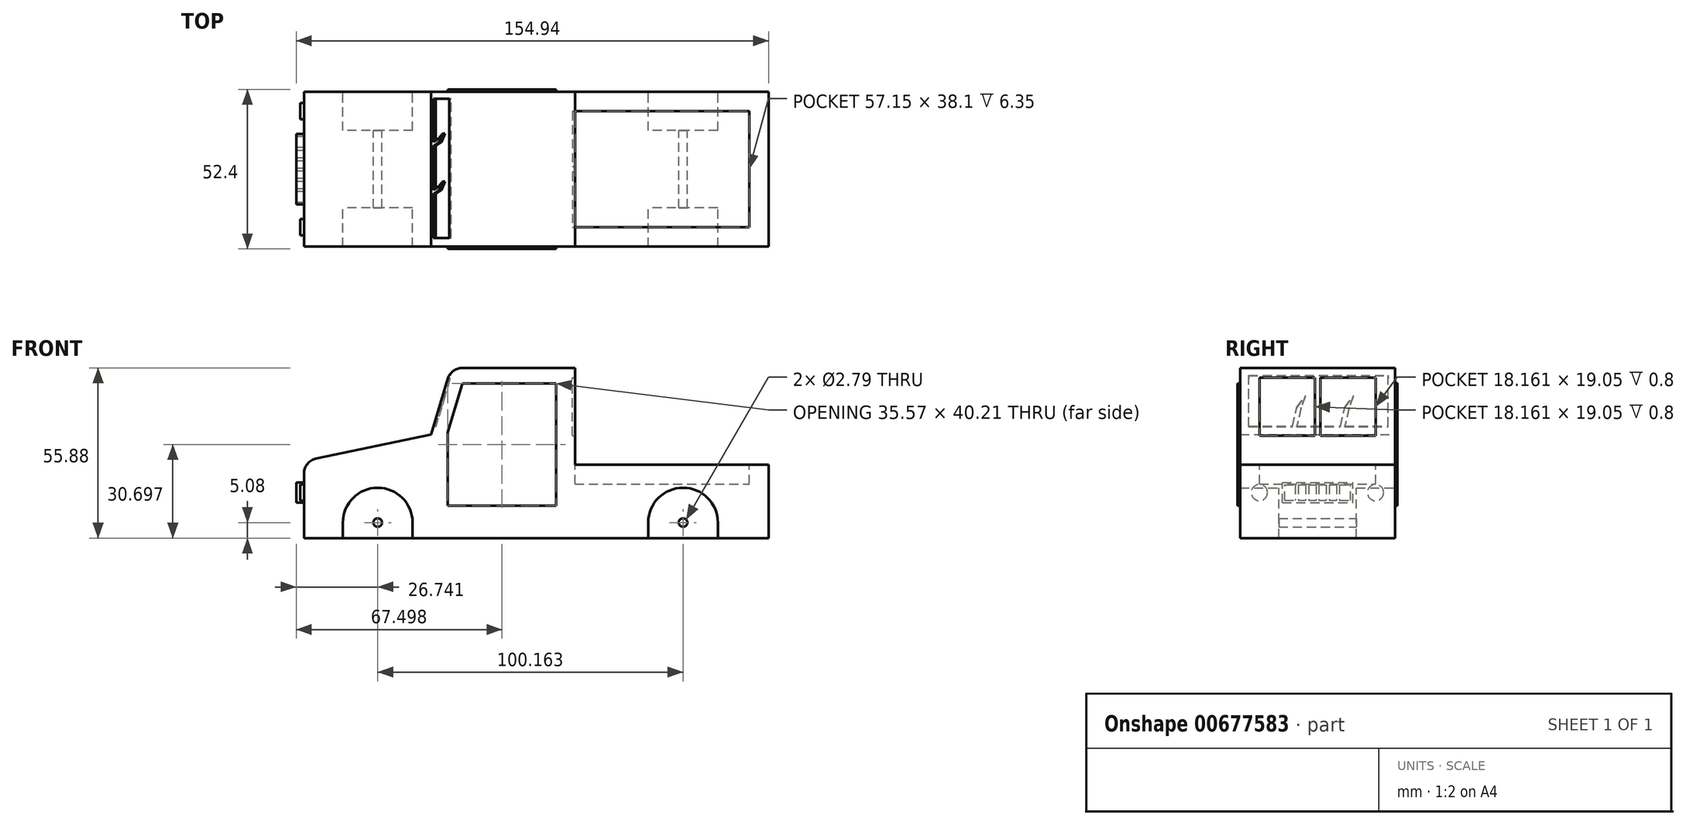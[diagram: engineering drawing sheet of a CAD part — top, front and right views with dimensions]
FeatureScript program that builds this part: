
annotation { "Feature Type Name" : "Feature", "Feature Type Description" : "" }
export const myFeature = defineFeature(function(context is Context, id is Id, definition is map)
    precondition{}
    {
        {
            var Q0;
            Q0=qCreatedBy(makeId("Front.planeOp"),FACE);
            var sketch = newSketch(context, id + "F0", { "sketchPlane" : qUnion([Q0])});
            skLineSegment(sketch, "E0", {"start": v(-68.75, 0) * mm, "end": v(83.65, 0) * mm});
            skLineSegment(sketch, "E1", {"start": v(83.65, 0) * mm, "end": v(83.65, 19.05) * mm});
            skLineSegment(sketch, "E2", {"start": v(83.65, 19.05) * mm, "end": v(20.15, 19.05) * mm});
            skLineSegment(sketch, "E3", {"start": v(20.15, 19.05) * mm, "end": v(20.15, 50.8) * mm});
            skLineSegment(sketch, "E4", {"start": v(20.15, 50.8) * mm, "end": v(-20.49, 50.8) * mm});
            skLineSegment(sketch, "E5", {"start": v(-20.49, 50.8) * mm, "end": v(-27.1, 28.92) * mm});
            skLineSegment(sketch, "E6", {"start": v(-68.75, 0) * mm, "end": v(-68.75, 20.2) * mm});
            skLineSegment(sketch, "E7", {"start": v(-68.75, 20.2) * mm, "end": v(-27.1, 28.92) * mm});
            skArc(sketch, "E8", {"start": v(-33.12, 0) * mm, "mid": v(-44.55, 11.43) * mm, "end": v(-55.98, 0) * mm});
            skArc(sketch, "E9", {"start": v(67.04, 0) * mm, "mid": v(55.61, 11.43) * mm, "end": v(44.18, 0) * mm});
            skSolve(sketch);
        }
        {
            var Q0;
            Q0 = qSketchRegion(id + "F0", true);
            extrude(context, id + "F1", {"entities" : qUnion([Q0]), "depth" : 50.8 * mm, "offsetDistance" : 25.4 * mm});
        }
        {
            var Q0;
            Q0=makeQuery(id+"F1.opExtrude","SWEPT_FACE",FACE,{"disambiguationData":[OSD([sQuery(id+"F0.wireOp",EDGE,"E2")])]});
            var sketch = newSketch(context, id + "F2", { "sketchPlane" : qUnion([Q0])});
            skLineSegment(sketch, "E10", {"start": v(20.15, -6.35) * mm, "end": v(77.3, -6.35) * mm});
            skLineSegment(sketch, "E11", {"start": v(77.3, -6.35) * mm, "end": v(77.3, -44.45) * mm});
            skLineSegment(sketch, "E12", {"start": v(77.3, -44.45) * mm, "end": v(20.15, -44.45) * mm});
            skLineSegment(sketch, "E13", {"start": v(20.15, -44.45) * mm, "end": v(20.15, -6.35) * mm});
            skSolve(sketch);
        }
        {
            var Q0;
            Q0=makeQuery(id+"F2.imprint","IMPRINT",FACE,{"disambiguationData":[TD([[makeQuery(id+"F2.imprint","IMPRINT",EDGE,{"derivedFrom":sQuery(id+"F2.wireOp",EDGE,"E10")}),-1.0]])]});
            extrude(context, id + "F3", {"entities" : qUnion([Q0]), "operationType" : NewBodyOperationType.REMOVE, "oppositeDirection" : true, "depth" : 6.35 * mm, "offsetDistance" : 25.4 * mm});
        }
        {
            var Q0;
            Q0=makeQuery(id+"F1.opExtrude","SWEPT_FACE",FACE,{"disambiguationData":[OSD([sQuery(id+"F0.wireOp",EDGE,"E6")])]});
            var sketch = newSketch(context, id + "F4", { "sketchPlane" : qUnion([Q0])});
            skCircle(sketch, "E14", {"center": v(6.35, 9.84) * mm, "radius": 2.67 * mm});
            skCircle(sketch, "E15", {"center": v(44.45, 9.84) * mm, "radius": 2.67 * mm});
            skLineSegment(sketch, "E16.bottom", {"start": v(36.96, 6.5) * mm, "end": v(13.84, 6.5) * mm});
            skLineSegment(sketch, "E16.top", {"start": v(36.96, 13.1) * mm, "end": v(13.84, 13.1) * mm});
            skLineSegment(sketch, "E16.left", {"start": v(36.96, 6.5) * mm, "end": v(36.96, 13.1) * mm});
            skLineSegment(sketch, "E16.right", {"start": v(13.84, 6.5) * mm, "end": v(13.84, 13.1) * mm});
            skPoint(sketch, "E16.middle", {"position": v(25.4, 9.8) * mm});
            skLineSegment(sketch, "E17.bottom", {"start": v(36.2, 7.27) * mm, "end": v(14.6, 7.27) * mm});
            skLineSegment(sketch, "E17.top", {"start": v(36.2, 12.35) * mm, "end": v(14.6, 12.35) * mm});
            skLineSegment(sketch, "E17.left", {"start": v(36.2, 7.27) * mm, "end": v(36.2, 12.35) * mm});
            skLineSegment(sketch, "E17.right", {"start": v(14.6, 7.27) * mm, "end": v(14.6, 12.35) * mm});
            skLineSegment(sketch, "E18", {"start": v(18.18, 12.35) * mm, "end": v(18.18, 7.27) * mm});
            skLineSegment(sketch, "E19", {"start": v(19.16, 12.35) * mm, "end": v(19.16, 7.27) * mm});
            skLineSegment(sketch, "E20.1.0.0", {"start": v(21.56, 12.35) * mm, "end": v(21.56, 7.27) * mm});
            skLineSegment(sketch, "E20.1.0.1", {"start": v(22.54, 12.35) * mm, "end": v(22.54, 7.27) * mm});
            skLineSegment(sketch, "E20.2.0.0", {"start": v(24.94, 12.35) * mm, "end": v(24.94, 7.27) * mm});
            skLineSegment(sketch, "E20.2.0.1", {"start": v(25.92, 12.35) * mm, "end": v(25.92, 7.27) * mm});
            skLineSegment(sketch, "E20.3.0.0", {"start": v(28.32, 12.35) * mm, "end": v(28.32, 7.27) * mm});
            skLineSegment(sketch, "E20.3.0.1", {"start": v(29.3, 12.35) * mm, "end": v(29.3, 7.27) * mm});
            skLineSegment(sketch, "E20.4.0.0", {"start": v(31.7, 12.35) * mm, "end": v(31.7, 7.27) * mm});
            skLineSegment(sketch, "E20.4.0.1", {"start": v(32.67, 12.35) * mm, "end": v(32.67, 7.27) * mm});
            skLineSegment(sketch, "E20.direction1", {"start": v(18.18, 7.27) * mm, "end": v(21.56, 7.27) * mm, "construction": true});
            skSolve(sketch);
        }
        {
            var Q0;
            Q0=makeQuery(id+"F4.imprint","IMPRINT",FACE,{"disambiguationData":[TD([[makeQuery(id+"F4.imprint","IMPRINT",EDGE,{"derivedFrom":sQuery(id+"F4.wireOp",EDGE,"E16.bottom")}),-1.0]])]});
            var Q1;
            {var subQ0=sQuery(id+"F4.wireOp",EDGE,"E18");Q1=makeQuery(id+"F4.imprint","IMPRINT",FACE,{"disambiguationData":[TD([[makeQuery(id+"F4.imprint","IMPRINT",EDGE,{"derivedFrom":subQ0}),1.0]])]});}
            var Q2;
            {var subQ0=sQuery(id+"F4.wireOp",EDGE,"E20.1.0.0");Q2=makeQuery(id+"F4.imprint","IMPRINT",FACE,{"disambiguationData":[TD([[makeQuery(id+"F4.imprint","IMPRINT",EDGE,{"derivedFrom":subQ0}),1.0]])]});}
            var Q3;
            {var subQ0=sQuery(id+"F4.wireOp",EDGE,"E20.2.0.0");Q3=makeQuery(id+"F4.imprint","IMPRINT",FACE,{"disambiguationData":[TD([[makeQuery(id+"F4.imprint","IMPRINT",EDGE,{"derivedFrom":subQ0}),1.0]])]});}
            var Q4;
            {var subQ0=sQuery(id+"F4.wireOp",EDGE,"E20.3.0.0");Q4=makeQuery(id+"F4.imprint","IMPRINT",FACE,{"disambiguationData":[TD([[makeQuery(id+"F4.imprint","IMPRINT",EDGE,{"derivedFrom":subQ0}),1.0]])]});}
            var Q5;
            {var subQ0=sQuery(id+"F4.wireOp",EDGE,"E20.4.0.0");Q5=makeQuery(id+"F4.imprint","IMPRINT",FACE,{"disambiguationData":[TD([[makeQuery(id+"F4.imprint","IMPRINT",EDGE,{"derivedFrom":subQ0}),1.0]])]});}
            extrude(context, id + "F5", {"entities" : qUnion([Q0, Q1, Q2, Q3, Q4, Q5]), "operationType" : NewBodyOperationType.ADD, "depth" : 2.54 * mm, "offsetDistance" : 25.4 * mm});
        }
        {
            var Q0;
            Q0=makeQuery(id+"F4.imprint","IMPRINT",FACE,{"disambiguationData":[TD([[makeQuery(id+"F4.imprint","IMPRINT",EDGE,{"derivedFrom":sQuery(id+"F4.wireOp",EDGE,"E14")}),1.0]])]});
            var Q1;
            Q1=makeQuery(id+"F4.imprint","IMPRINT",FACE,{"disambiguationData":[TD([[makeQuery(id+"F4.imprint","IMPRINT",EDGE,{"derivedFrom":sQuery(id+"F4.wireOp",EDGE,"E15")}),1.0]])]});
            extrude(context, id + "F6", {"entities" : qUnion([Q0, Q1]), "operationType" : NewBodyOperationType.ADD, "depth" : 1.27 * mm, "offsetDistance" : 25.4 * mm});
        }
        {
            var Q0;
            Q0=makeQuery(id+"F1.opExtrude","SWEPT_FACE",FACE,{"disambiguationData":[OSD([sQuery(id+"F0.wireOp",EDGE,"E5")])]});
            var sketch = newSketch(context, id + "F7", { "sketchPlane" : qUnion([Q0])});
            skLineSegment(sketch, "E21.bottom", {"start": v(47.98, 22.7) * mm, "end": v(2.26, 22.7) * mm});
            skLineSegment(sketch, "E21.top", {"start": v(47.98, 40.22) * mm, "end": v(2.26, 40.22) * mm});
            skLineSegment(sketch, "E21.left", {"start": v(47.98, 22.7) * mm, "end": v(47.98, 40.22) * mm});
            skLineSegment(sketch, "E21.right", {"start": v(2.26, 22.7) * mm, "end": v(2.26, 40.22) * mm});
            skPoint(sketch, "E21.middle", {"position": v(25.12, 31.46) * mm});
            skLineSegment(sketch, "E22", {"start": v(33.56, 22.7) * mm, "end": v(32.22, 29.14) * mm});
            skLineSegment(sketch, "E23", {"start": v(32.22, 29.14) * mm, "end": v(29.43, 33.12) * mm});
            skLineSegment(sketch, "E24", {"start": v(29.43, 33.12) * mm, "end": v(30.82, 29.14) * mm});
            skPoint(sketch, "E24.endSnap0", {"position": v(30.82, 31.13) * mm});
            skLineSegment(sketch, "E25", {"start": v(30.82, 29.14) * mm, "end": v(32.22, 22.7) * mm});
            skLineSegment(sketch, "E26.1.0.0", {"start": v(17.81, 22.7) * mm, "end": v(16.47, 29.14) * mm});
            skLineSegment(sketch, "E26.1.0.1", {"start": v(16.47, 29.14) * mm, "end": v(13.68, 33.12) * mm});
            skLineSegment(sketch, "E26.1.0.2", {"start": v(13.68, 33.12) * mm, "end": v(15.08, 29.14) * mm});
            skLineSegment(sketch, "E26.1.0.3", {"start": v(15.08, 29.14) * mm, "end": v(16.47, 22.7) * mm});
            skLineSegment(sketch, "E26.direction1", {"start": v(33.56, 22.7) * mm, "end": v(17.81, 22.7) * mm, "construction": true});
            skSolve(sketch);
        }
        {
            var Q0;
            Q0=makeQuery(id+"F7.imprint","IMPRINT",FACE,{"disambiguationData":[TD([[makeQuery(id+"F7.imprint","IMPRINT",EDGE,{"derivedFrom":sQuery(id+"F7.wireOp",EDGE,"E21.top")}),1.0]])]});
            extrude(context, id + "F8", {"entities" : qUnion([Q0]), "operationType" : NewBodyOperationType.REMOVE, "oppositeDirection" : true, "depth" : 0.8 * mm, "offsetDistance" : 25.4 * mm});
        }
        {
            var Q0;
            Q0=makeQuery(id+"F1.opExtrude","SWEPT_EDGE",EDGE,{"disambiguationData":[OSD([sQuery(id+"F0.wireOp",EDGE,"E6"),sQuery(id+"F0.wireOp",EDGE,"E7")])]});
            var Q1;
            Q1=makeQuery(id+"F1.opExtrude","SWEPT_EDGE",EDGE,{"disambiguationData":[OSD([sQuery(id+"F0.wireOp",EDGE,"E4"),sQuery(id+"F0.wireOp",EDGE,"E5")])]});
            fillet(context, id + "F9", {"entities" : qUnion([Q0, Q1]), "radius" : 5.08 * mm, "tangentPropagation" : true, "allowEdgeOverflow" : false});
        }
        {
            var Q0;
            Q0=makeQuery(id+"F1.opExtrude","CAP_FACE",FACE,{"disambiguationData":[OSD([sQuery(id+"F0.wireOp",EDGE,"E0"),sQuery(id+"F0.wireOp",EDGE,"E1"),sQuery(id+"F0.wireOp",EDGE,"E2"),sQuery(id+"F0.wireOp",EDGE,"E3"),sQuery(id+"F0.wireOp",EDGE,"E4"),sQuery(id+"F0.wireOp",EDGE,"E5"),sQuery(id+"F0.wireOp",EDGE,"E6"),sQuery(id+"F0.wireOp",EDGE,"E7")])],"isStart":false});
            var sketch = newSketch(context, id + "F10", { "sketchPlane" : qUnion([Q0])});
            skLineSegment(sketch, "E27", {"start": v(-16.71, 45.72) * mm, "end": v(-21.58, 29.64) * mm});
            skLineSegment(sketch, "E28", {"start": v(-21.58, 29.64) * mm, "end": v(-21.58, 5.51) * mm});
            skLineSegment(sketch, "E29", {"start": v(-21.58, 5.51) * mm, "end": v(13.98, 5.51) * mm});
            skLineSegment(sketch, "E30", {"start": v(13.98, 5.51) * mm, "end": v(14, 45.72) * mm});
            skLineSegment(sketch, "E31", {"start": v(-16.71, 45.72) * mm, "end": v(14, 45.72) * mm});
            skSolve(sketch);
        }
        {
            var Q0;
            Q0=makeQuery(id+"F10.imprint","IMPRINT",FACE,{"disambiguationData":[TD([[makeQuery(id+"F10.imprint","IMPRINT",EDGE,{"derivedFrom":sQuery(id+"F10.wireOp",EDGE,"E27")}),1.0]])]});
            extrude(context, id + "F11", {"entities" : qUnion([Q0]), "operationType" : NewBodyOperationType.ADD, "depth" : 0.8 * mm, "offsetDistance" : 25.4 * mm});
        }
        {
            var Q0;
            Q0=makeQuery(id+"F1.opExtrude","CAP_FACE",FACE,{"disambiguationData":[OSD([sQuery(id+"F0.wireOp",EDGE,"E0"),sQuery(id+"F0.wireOp",EDGE,"E1"),sQuery(id+"F0.wireOp",EDGE,"E2"),sQuery(id+"F0.wireOp",EDGE,"E3"),sQuery(id+"F0.wireOp",EDGE,"E4"),sQuery(id+"F0.wireOp",EDGE,"E5"),sQuery(id+"F0.wireOp",EDGE,"E6"),sQuery(id+"F0.wireOp",EDGE,"E7")])],"isStart":true});
            var sketch = newSketch(context, id + "F12", { "sketchPlane" : qUnion([Q0])});
            skLineSegment(sketch, "E32", {"start": v(16.71, 45.72) * mm, "end": v(21.57, 29.65) * mm});
            skLineSegment(sketch, "E33", {"start": v(21.57, 29.65) * mm, "end": v(21.57, 5.52) * mm});
            skLineSegment(sketch, "E34", {"start": v(21.57, 5.52) * mm, "end": v(-14, 5.52) * mm});
            skLineSegment(sketch, "E35", {"start": v(-14, 5.52) * mm, "end": v(-14, 45.72) * mm});
            skLineSegment(sketch, "E36", {"start": v(-14, 45.72) * mm, "end": v(16.71, 45.72) * mm});
            skSolve(sketch);
        }
        {
            var Q0;
            Q0=makeQuery(id+"F12.imprint","IMPRINT",FACE,{"disambiguationData":[TD([[makeQuery(id+"F12.imprint","IMPRINT",EDGE,{"derivedFrom":sQuery(id+"F12.wireOp",EDGE,"E32")}),-1.0]])]});
            extrude(context, id + "F13", {"entities" : qUnion([Q0]), "operationType" : NewBodyOperationType.ADD, "depth" : 0.8 * mm, "offsetDistance" : 25.4 * mm});
        }
        {
            var Q0;
            Q0=makeQuery(id+"F13.opExtrude","CAP_FACE",FACE,{"disambiguationData":[OSD([sQuery(id+"F12.wireOp",EDGE,"E32"),sQuery(id+"F12.wireOp",EDGE,"E33"),sQuery(id+"F12.wireOp",EDGE,"E34"),sQuery(id+"F12.wireOp",EDGE,"E35"),sQuery(id+"F12.wireOp",EDGE,"E36")])],"isStart":false});
            var sketch = newSketch(context, id + "F14", { "sketchPlane" : qUnion([Q0])});
            skLineSegment(sketch, "E37", {"start": v(18.82, 29.65) * mm, "end": v(14.9, 43.16) * mm});
            skLineSegment(sketch, "E38", {"start": v(14.9, 43.16) * mm, "end": v(-11.56, 43.16) * mm});
            skLineSegment(sketch, "E39", {"start": v(-11.56, 43.16) * mm, "end": v(-11.56, 29.65) * mm});
            skLineSegment(sketch, "E40", {"start": v(-11.56, 29.65) * mm, "end": v(18.82, 29.65) * mm});
            skLineSegment(sketch, "E41.bottom", {"start": v(-11.56, 22.39) * mm, "end": v(-7, 22.39) * mm});
            skLineSegment(sketch, "E41.top", {"start": v(-11.56, 20.6) * mm, "end": v(-7, 20.6) * mm});
            skLineSegment(sketch, "E41.left", {"start": v(-11.56, 22.39) * mm, "end": v(-11.56, 20.6) * mm});
            skLineSegment(sketch, "E41.right", {"start": v(-7, 22.39) * mm, "end": v(-7, 20.6) * mm});
            skSolve(sketch);
        }
        {
            var Q0;
            Q0=makeQuery(id+"F14.imprint","IMPRINT",FACE,{"disambiguationData":[TD([[makeQuery(id+"F14.imprint","IMPRINT",EDGE,{"derivedFrom":sQuery(id+"F14.wireOp",EDGE,"E37")}),1.0]])]});
            extrude(context, id + "F15", {"entities" : qUnion([Q0]), "operationType" : NewBodyOperationType.ADD, "oppositeDirection" : true, "depth" : 0.25 * mm, "offsetDistance" : 25.4 * mm});
        }
        {
            var Q0;
            Q0=makeQuery(id+"F3.boolean.opBoolean","MERGE",FACE,{"derivedFrom":[makeQuery(id+"F1.opExtrude","SWEPT_FACE",FACE,{"disambiguationData":[OSD([sQuery(id+"F0.wireOp",EDGE,"E3")])]}),makeQuery(id+"F3.opExtrude","SWEPT_FACE",FACE,{"disambiguationData":[OSD([sQuery(id+"F2.wireOp",EDGE,"E13")])]})]});
            var sketch = newSketch(context, id + "F16", { "sketchPlane" : qUnion([Q0])});
            skLineSegment(sketch, "E42.bottom", {"start": v(-6.35, 28.57) * mm, "end": v(-44.45, 28.57) * mm});
            skLineSegment(sketch, "E42.top", {"start": v(-6.35, 47.62) * mm, "end": v(-44.45, 47.62) * mm});
            skLineSegment(sketch, "E42.left", {"start": v(-6.35, 28.57) * mm, "end": v(-6.35, 47.62) * mm});
            skLineSegment(sketch, "E42.right", {"start": v(-44.45, 28.57) * mm, "end": v(-44.45, 47.62) * mm});
            skPoint(sketch, "E42.middle", {"position": v(-25.4, 38.1) * mm});
            skLineSegment(sketch, "E43.bottom", {"start": v(-24.51, 28.57) * mm, "end": v(-26.29, 28.57) * mm});
            skLineSegment(sketch, "E43.top", {"start": v(-24.51, 47.62) * mm, "end": v(-26.29, 47.62) * mm});
            skLineSegment(sketch, "E43.left", {"start": v(-24.51, 28.57) * mm, "end": v(-24.51, 47.62) * mm});
            skLineSegment(sketch, "E43.right", {"start": v(-26.29, 28.57) * mm, "end": v(-26.29, 47.62) * mm});
            skSolve(sketch);
        }
        {
            var Q0;
            {var subQ0=sQuery(id+"F16.wireOp",EDGE,"E42.right");Q0=makeQuery(id+"F16.imprint","IMPRINT",FACE,{"disambiguationData":[TD([[makeQuery(id+"F16.imprint","IMPRINT",EDGE,{"derivedFrom":subQ0}),-1.0]])]});}
            var Q1;
            {var subQ0=sQuery(id+"F16.wireOp",EDGE,"E42.left");Q1=makeQuery(id+"F16.imprint","IMPRINT",FACE,{"disambiguationData":[TD([[makeQuery(id+"F16.imprint","IMPRINT",EDGE,{"derivedFrom":subQ0}),1.0]])]});}
            extrude(context, id + "F17", {"entities" : qUnion([Q0, Q1]), "operationType" : NewBodyOperationType.REMOVE, "oppositeDirection" : true, "depth" : 0.8 * mm, "offsetDistance" : 25.4 * mm});
        }
        {
            var Q0;
            {var subQ0=sQuery(id+"F0.wireOp",EDGE,"E9");Q0=makeQuery(id+"F0.imprint","IMPRINT",FACE,{"disambiguationData":[TD([[makeQuery(id+"F0.imprint","IMPRINT",EDGE,{"derivedFrom":subQ0}),1.0]])]});}
            var Q1;
            {var subQ0=sQuery(id+"F0.wireOp",EDGE,"E8");Q1=makeQuery(id+"F0.imprint","IMPRINT",FACE,{"disambiguationData":[TD([[makeQuery(id+"F0.imprint","IMPRINT",EDGE,{"derivedFrom":subQ0}),1.0]])]});}
            extrude(context, id + "F18", {"entities" : qUnion([Q0, Q1]), "operationType" : NewBodyOperationType.REMOVE, "depth" : 50.8 * mm, "offsetDistance" : 25.4 * mm});
        }
        {
            var Q0;
            {var subQ0=sQuery(id+"F0.wireOp",EDGE,"E7");var subQ1=sQuery(id+"F0.wireOp",EDGE,"E6");var subQ2=sQuery(id+"F0.wireOp",EDGE,"E5");var subQ3=sQuery(id+"F0.wireOp",EDGE,"E4");var subQ4=sQuery(id+"F0.wireOp",EDGE,"E3");var subQ5=sQuery(id+"F0.wireOp",EDGE,"E2");var subQ6=sQuery(id+"F0.wireOp",EDGE,"E1");var subQ7=sQuery(id+"F0.wireOp",EDGE,"E0");Q0=makeQuery(id+"F18.boolean.opBoolean","SPLIT",FACE,{"disambiguationData":[TD([makeQuery(id+"F1.opExtrude","CAP_FACE",FACE,{"disambiguationData":[OSD([subQ7,subQ6,subQ5,subQ4,subQ3,subQ2,subQ1,subQ0])],"isStart":true}),makeQuery(id+"F1.opExtrude","CAP_FACE",FACE,{"disambiguationData":[OSD([subQ7,subQ6,subQ5,subQ4,subQ3,subQ2,subQ1,subQ0])],"isStart":false}),makeQuery(id+"F1.opExtrude","SWEPT_FACE",FACE,{"disambiguationData":[OSD([subQ1])]}),makeQuery(id+"F18.opExtrude","SWEPT_FACE",FACE,{"disambiguationData":[OSD([sQuery(id+"F0.wireOp",EDGE,"E8")])]})])],"derivedFrom":makeQuery(id+"F1.opExtrude","SWEPT_FACE",FACE,{"disambiguationData":[OSD([subQ7])]})});}
            var sketch = newSketch(context, id + "F19", { "sketchPlane" : qUnion([Q0])});
            skLineSegment(sketch, "E44.bottom", {"start": v(69.82, 12.7) * mm, "end": v(-57.18, 12.7) * mm});
            skLineSegment(sketch, "E44.top", {"start": v(69.82, 38.1) * mm, "end": v(-57.18, 38.1) * mm});
            skLineSegment(sketch, "E44.left", {"start": v(69.82, 12.7) * mm, "end": v(69.82, 38.1) * mm});
            skLineSegment(sketch, "E44.right", {"start": v(-57.18, 12.7) * mm, "end": v(-57.18, 38.1) * mm});
            skPoint(sketch, "E44.middle", {"position": v(6.32, 25.4) * mm});
            skSolve(sketch);
        }
        {
            var Q0;
            Q0 = qSketchRegion(id + "F19", true);
            extrude(context, id + "F20", {"entities" : qUnion([Q0]), "operationType" : NewBodyOperationType.ADD, "oppositeDirection" : true, "depth" : 12.7 * mm, "offsetDistance" : 25.4 * mm});
        }
        {
            var Q0;
            {var subQ0=sQuery(id+"F0.wireOp",EDGE,"E7");var subQ1=sQuery(id+"F0.wireOp",EDGE,"E6");var subQ2=sQuery(id+"F0.wireOp",EDGE,"E5");var subQ3=sQuery(id+"F0.wireOp",EDGE,"E4");var subQ4=sQuery(id+"F0.wireOp",EDGE,"E3");var subQ5=sQuery(id+"F0.wireOp",EDGE,"E2");var subQ6=sQuery(id+"F0.wireOp",EDGE,"E1");var subQ7=sQuery(id+"F0.wireOp",EDGE,"E0");var subQ8=makeQuery(id+"F1.opExtrude","CAP_FACE",FACE,{"disambiguationData":[OSD([subQ7,subQ6,subQ5,subQ4,subQ3,subQ2,subQ1,subQ0])],"isStart":true});var subQ9=makeQuery(id+"F1.opExtrude","CAP_FACE",FACE,{"disambiguationData":[OSD([subQ7,subQ6,subQ5,subQ4,subQ3,subQ2,subQ1,subQ0])],"isStart":false});var subQ10=makeQuery(id+"F18.opExtrude","SWEPT_FACE",FACE,{"disambiguationData":[OSD([sQuery(id+"F0.wireOp",EDGE,"E8")])]});var subQ11=makeQuery(id+"F18.opExtrude","SWEPT_FACE",FACE,{"disambiguationData":[OSD([sQuery(id+"F0.wireOp",EDGE,"E9")])]});var subQ12=makeQuery(id+"F1.opExtrude","SWEPT_FACE",FACE,{"disambiguationData":[OSD([subQ7])]});Q0=makeQuery(id+"F20.boolean.opBoolean","MERGE",FACE,{"derivedFrom":[makeQuery(id+"F18.boolean.opBoolean","SPLIT",FACE,{"disambiguationData":[TD([subQ8,subQ9,makeQuery(id+"F1.opExtrude","SWEPT_FACE",FACE,{"disambiguationData":[OSD([subQ1])]}),subQ10])],"derivedFrom":subQ12}),makeQuery(id+"F18.boolean.opBoolean","SPLIT",FACE,{"disambiguationData":[TD([subQ8,subQ9,makeQuery(id+"F1.opExtrude","SWEPT_FACE",FACE,{"disambiguationData":[OSD([subQ6])]}),subQ11])],"derivedFrom":subQ12}),makeQuery(id+"F18.boolean.opBoolean","SPLIT",FACE,{"disambiguationData":[TD([subQ8,subQ9,subQ10,subQ11])],"derivedFrom":subQ12}),makeQuery(id+"F20.opExtrude","CAP_FACE",FACE,{"disambiguationData":[OSD([sQuery(id+"F19.wireOp",EDGE,"E44.bottom"),sQuery(id+"F19.wireOp",EDGE,"E44.top"),sQuery(id+"F19.wireOp",EDGE,"E44.left"),sQuery(id+"F19.wireOp",EDGE,"E44.right")])],"isStart":true})]});}
            extrude(context, id + "F21", {"entities" : qUnion([Q0]), "operationType" : NewBodyOperationType.ADD, "depth" : 5.08 * mm, "offsetDistance" : 25.4 * mm});
        }
        {
            var Q0;
            {var subQ1=makeQuery(id+"F18.boolean.opBoolean","COPY",FACE,{"derivedFrom":makeQuery(id+"F18.opExtrude","SWEPT_FACE",FACE,{"disambiguationData":[OSD([sQuery(id+"F0.wireOp",EDGE,"E9")])]})});var subQ2=sQuery(id+"F19.wireOp",EDGE,"E44.bottom");var subQ3=makeQuery(id+"F20.opExtrude","SWEPT_FACE",FACE,{"disambiguationData":[OSD([subQ2])]});Q0=makeQuery(id+"F21.boolean.opBoolean","MERGE",FACE,{"derivedFrom":[makeQuery(id+"F20.boolean.opBoolean","SPLIT",FACE,{"disambiguationData":[TD([subQ1])],"derivedFrom":subQ3}),makeQuery(id+"F21.opExtrude","SWEPT_FACE",FACE,{"disambiguationData":[OSD([subQ2]),TDD([makeQuery(id+"F20.boolean.opBoolean","SPLIT",EDGE,{"disambiguationData":[TD([subQ1])],"derivedFrom":makeQuery(id+"F20.opExtrude","CAP_EDGE",EDGE,{"disambiguationData":[OSD([subQ2])],"isStart":true})})])]})]});}
            var sketch = newSketch(context, id + "F22", { "sketchPlane" : qUnion([Q0])});
            skCircle(sketch, "E45", {"center": v(-55.61, 0) * mm, "radius": 1.4 * mm});
            skSolve(sketch);
        }
        {
            var Q0;
            {var subQ1=makeQuery(id+"F18.boolean.opBoolean","COPY",FACE,{"derivedFrom":makeQuery(id+"F18.opExtrude","SWEPT_FACE",FACE,{"disambiguationData":[OSD([sQuery(id+"F0.wireOp",EDGE,"E8")])]})});var subQ2=sQuery(id+"F19.wireOp",EDGE,"E44.bottom");var subQ3=makeQuery(id+"F20.opExtrude","SWEPT_FACE",FACE,{"disambiguationData":[OSD([subQ2])]});Q0=makeQuery(id+"F21.boolean.opBoolean","MERGE",FACE,{"derivedFrom":[makeQuery(id+"F20.boolean.opBoolean","SPLIT",FACE,{"disambiguationData":[TD([subQ1])],"derivedFrom":subQ3}),makeQuery(id+"F21.opExtrude","SWEPT_FACE",FACE,{"disambiguationData":[OSD([subQ2]),TDD([makeQuery(id+"F20.boolean.opBoolean","SPLIT",EDGE,{"disambiguationData":[TD([subQ1])],"derivedFrom":makeQuery(id+"F20.opExtrude","CAP_EDGE",EDGE,{"disambiguationData":[OSD([subQ2])],"isStart":true})})])]})]});}
            var sketch = newSketch(context, id + "F23", { "sketchPlane" : qUnion([Q0])});
            skCircle(sketch, "E46", {"center": v(44.55, 0) * mm, "radius": 1.4 * mm});
            skSolve(sketch);
        }
        {
            var Q0;
            Q0=makeQuery(id+"F22.imprint","IMPRINT",FACE,{"disambiguationData":[TD([[makeQuery(id+"F22.imprint","IMPRINT",EDGE,{"derivedFrom":sQuery(id+"F22.wireOp",EDGE,"E45")}),1.0]])]});
            var Q1;
            Q1=makeQuery(id+"F23.imprint","IMPRINT",FACE,{"disambiguationData":[TD([[makeQuery(id+"F23.imprint","IMPRINT",EDGE,{"derivedFrom":sQuery(id+"F23.wireOp",EDGE,"E46")}),1.0]])]});
            extrude(context, id + "F24", {"entities" : qUnion([Q0, Q1]), "operationType" : NewBodyOperationType.REMOVE, "oppositeDirection" : true, "depth" : 25.4 * mm, "offsetDistance" : 25.4 * mm});
        }
    });
